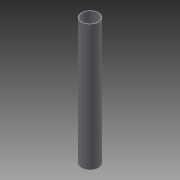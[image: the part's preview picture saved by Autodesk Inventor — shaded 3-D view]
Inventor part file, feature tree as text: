
AUTODESK INVENTOR PART (.ipt)
format: ipt  version: 2015 (Build 190159000, 159)  size: 69,632 bytes
history: native  units: mm
features: extrude x1, sketch x1
ambient origin geometry x8: Origin, YZ Plane, XZ Plane, XY Plane, X Axis, Y Axis, Z Axis, Center Point
bodies: Solid1 (feature_tree)
feature tree (2):
  extrude  "Extrusion1"  Depth=233.0mm
  sketch  "Sketch1"  dims[d0=31.75mm d1=28.575mm d2=233.0mm d3=0.0mm]
